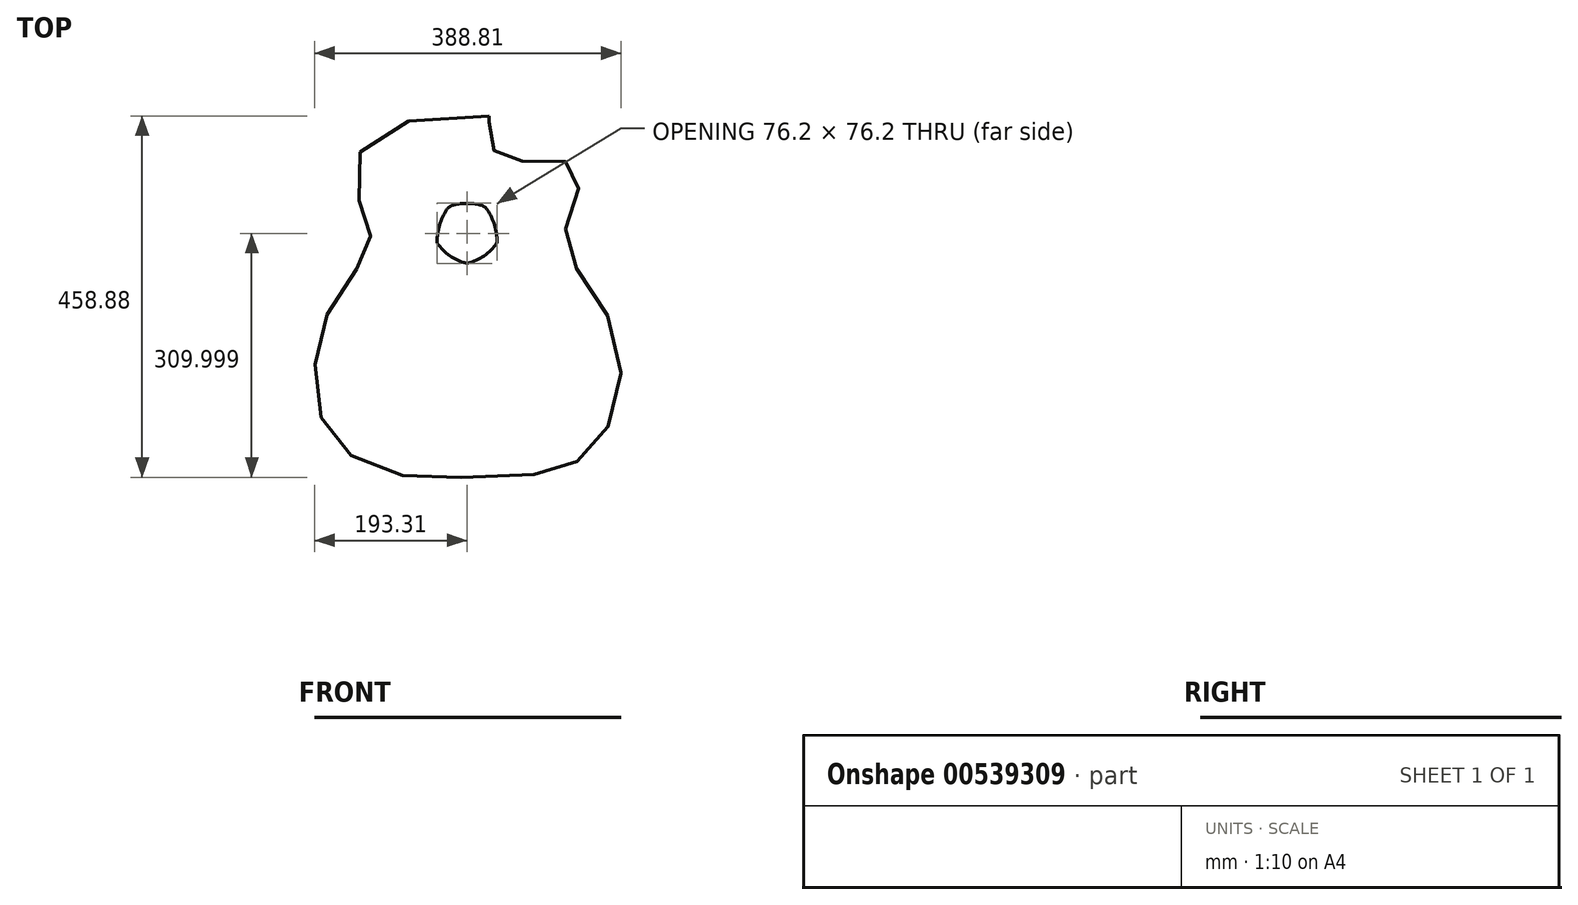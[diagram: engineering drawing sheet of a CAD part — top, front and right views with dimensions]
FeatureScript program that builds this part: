
annotation { "Feature Type Name" : "Feature", "Feature Type Description" : "" }
export const myFeature = defineFeature(function(context is Context, id is Id, definition is map)
    precondition{}
    {
        {
            var Q0;
            Q0=qCreatedBy(makeId("Top.planeOp"),FACE);
            var sketch = newSketch(context, id + "F0", { "sketchPlane" : qUnion([Q0])});
            skCircle(sketch, "E0", {"center": v(0, 0) * mm, "radius": 25.4 * mm, "construction": true});
            skPoint(sketch, "E1", {"position": v(0, 25.4) * mm});
            skLineSegment(sketch, "E2", {"start": v(-13.4, 25.4) * mm, "end": v(13.4, 25.4) * mm, "construction": true});
            skLineSegment(sketch, "E3", {"start": v(-13.4, 25.4) * mm, "end": v(-35.92, -7.54) * mm, "construction": true});
            skLineSegment(sketch, "E4", {"start": v(-35.92, -7.54) * mm, "end": v(0, -29.93) * mm, "construction": true});
            skLineSegment(sketch, "E5", {"start": v(0, -29.93) * mm, "end": v(35.92, -7.54) * mm, "construction": true});
            skLineSegment(sketch, "E6", {"start": v(35.92, -7.54) * mm, "end": v(13.4, 25.4) * mm, "construction": true});
            skArc(sketch, "E7", {"start": v(-25.64, 33.57) * mm, "mid": v(-21.83, 37.46) * mm, "end": v(-16.87, 39.7) * mm});
            skArc(sketch, "E8", {"start": v(-16.87, 39.7) * mm, "mid": v(0, 41.7) * mm, "end": v(16.87, 39.7) * mm});
            skArc(sketch, "E9", {"start": v(16.87, 39.7) * mm, "mid": v(21.83, 37.46) * mm, "end": v(25.64, 33.57) * mm});
            skArc(sketch, "E10", {"start": v(25.64, 33.57) * mm, "mid": v(34.92, 13.94) * mm, "end": v(38.1, -7.54) * mm});
            skArc(sketch, "E11", {"start": v(38.1, -7.54) * mm, "mid": v(38, -8.17) * mm, "end": v(37.73, -8.75) * mm});
            skArc(sketch, "E12", {"start": v(37.73, -8.75) * mm, "mid": v(21.81, -25) * mm, "end": v(1.07, -34.36) * mm});
            skArc(sketch, "E13", {"start": v(1.07, -34.36) * mm, "mid": v(0, -34.5) * mm, "end": v(-1.07, -34.36) * mm});
            skArc(sketch, "E14", {"start": v(-1.07, -34.36) * mm, "mid": v(-21.81, -25) * mm, "end": v(-37.73, -8.75) * mm});
            skArc(sketch, "E15", {"start": v(-37.73, -8.75) * mm, "mid": v(-38, -8.17) * mm, "end": v(-38.1, -7.54) * mm});
            skArc(sketch, "E16", {"start": v(-38.1, -7.54) * mm, "mid": v(-34.92, 13.94) * mm, "end": v(-25.64, 33.57) * mm});
            skSolve(sketch);
        }
        {
            var Q0;
            Q0=qCreatedBy(makeId("Top.planeOp"),FACE);
            var sketch = newSketch(context, id + "F1", { "sketchPlane" : qUnion([Q0])});
            skFitSpline(sketch, "E17", {"points": [v(27.99, 152.5) * mm, v(-102.66, 137.01) * mm, v(-141.59, 89.5) * mm, v(-134.99, 38.04) * mm, v(-124.43, 9) * mm, v(-123.77, -16.73) * mm, v(-143.57, -45.76) * mm, v(-179.86, -104.48) * mm, v(-193.05, -161.23) * mm, v(-186.45, -225.89) * mm, v(-160.06, -269.44) * mm, v(-96.72, -301.1) * mm, v(-34.04, -306.39) * mm, v(84.73, -303.09) * mm, v(130.92, -291.21) * mm, v(163.91, -265.48) * mm, v(192.28, -206.1) * mm, v(190.3, -136.81) * mm, v(156.65, -62.25) * mm, v(125.64, -20.69) * mm, v(128.28, 18.9) * mm, v(141.48, 56.51) * mm, v(136.2, 86.87) * mm, v(123.66, 94.78) * mm, v(77.47, 95.44) * mm, v(52.4, 96.76) * mm, v(34.59, 107.98) * mm, v(27.99, 130.41) * mm, v(27.99, 144.93) * mm], "startDerivative": vector(-2505.75, -25.96) * mm, "endDerivative": vector(32.82, 681.48) * mm});
            skLineSegment(sketch, "E18", {"start": v(27.99, 144.93) * mm, "end": v(27.99, 152.5) * mm});
            skLineSegment(sketch, "E19", {"start": v(-193.3, -67.24) * mm, "end": v(-193.3, -265.71) * mm, "construction": true});
            skLineSegment(sketch, "E20", {"start": v(195.5, -62.92) * mm, "end": v(195.5, -279.38) * mm, "construction": true});
            skLineSegment(sketch, "E21", {"start": v(-169, 152.5) * mm, "end": v(105, 152.5) * mm, "construction": true});
            skLineSegment(sketch, "E22", {"start": v(-170.96, -306.4) * mm, "end": v(217.65, -306.4) * mm, "construction": true});
            skSolve(sketch);
        }
        {
            var Q0;
            Q0 = qSketchRegion(id + "F1", true);
            extrude(context, id + "F2", {"entities" : qUnion([Q0]), "oppositeDirection" : true, "depth" : 1 / 203.2 * mm, "offsetDistance" : 25.4 * mm});
        }
        {
            var Q0;
            Q0 = qSketchRegion(id + "F0", true);
            extrude(context, id + "F3", {"entities" : qUnion([Q0]), "operationType" : NewBodyOperationType.REMOVE, "oppositeDirection" : true, "depth" : 25.4 * mm, "offsetDistance" : 25.4 * mm});
        }
    });
